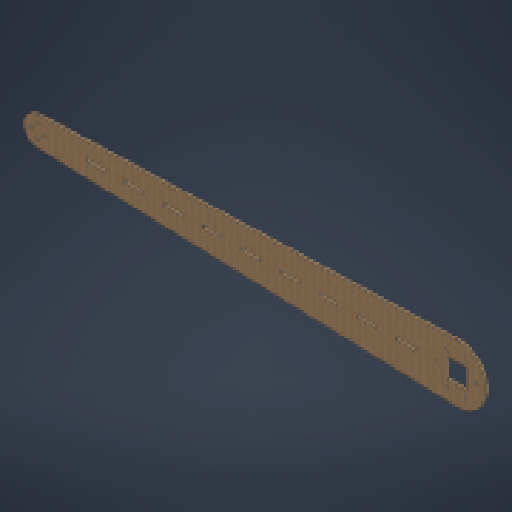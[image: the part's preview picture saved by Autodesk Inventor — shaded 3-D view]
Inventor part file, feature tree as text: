
AUTODESK INVENTOR PART (.ipt)
format: ipt  version: 2024.1 (Build 281209000, 209)  size: 221,696 bytes
history: native  units: in
note: dims shown in document units (in); Inventor stores cm internally (conversion verified against a paired STEP export)
features: other x3, extrude x1, sketch x1, reference x1
ambient origin geometry x8: Origin, YZ Plane, XZ Plane, XY Plane, X Axis, Y Axis, Z Axis, Center Point
bodies: Solid1 (feature_tree)
feature tree (6):
  extrude  "Extrusion1"  Depth=21.6535in
  sketch  "Sketch1"  dims[d0=3.0in d1=21.6535in d2=1.5in d3=0.1575in d4=0.375in d5=1.5748in d7=360.0deg d9=0.1575in d10=0.1575in d11=0.1575in d12=0.1575in d13=0.1575in d14=0.1575in d15=0.125in d16=0.0in d17=1.0in d18=0.125in d19=3.0in d20=3.5433in d22=2.0in d23=0.3937in d25=1.0in]
  reference  "Reference1"
  other  "<userpath>\Documents\School\FallCAD\Trebuchet\Trebuchet.iam"
  other  "Trebuchet.iam"
  other  "ArmPivot:1"
